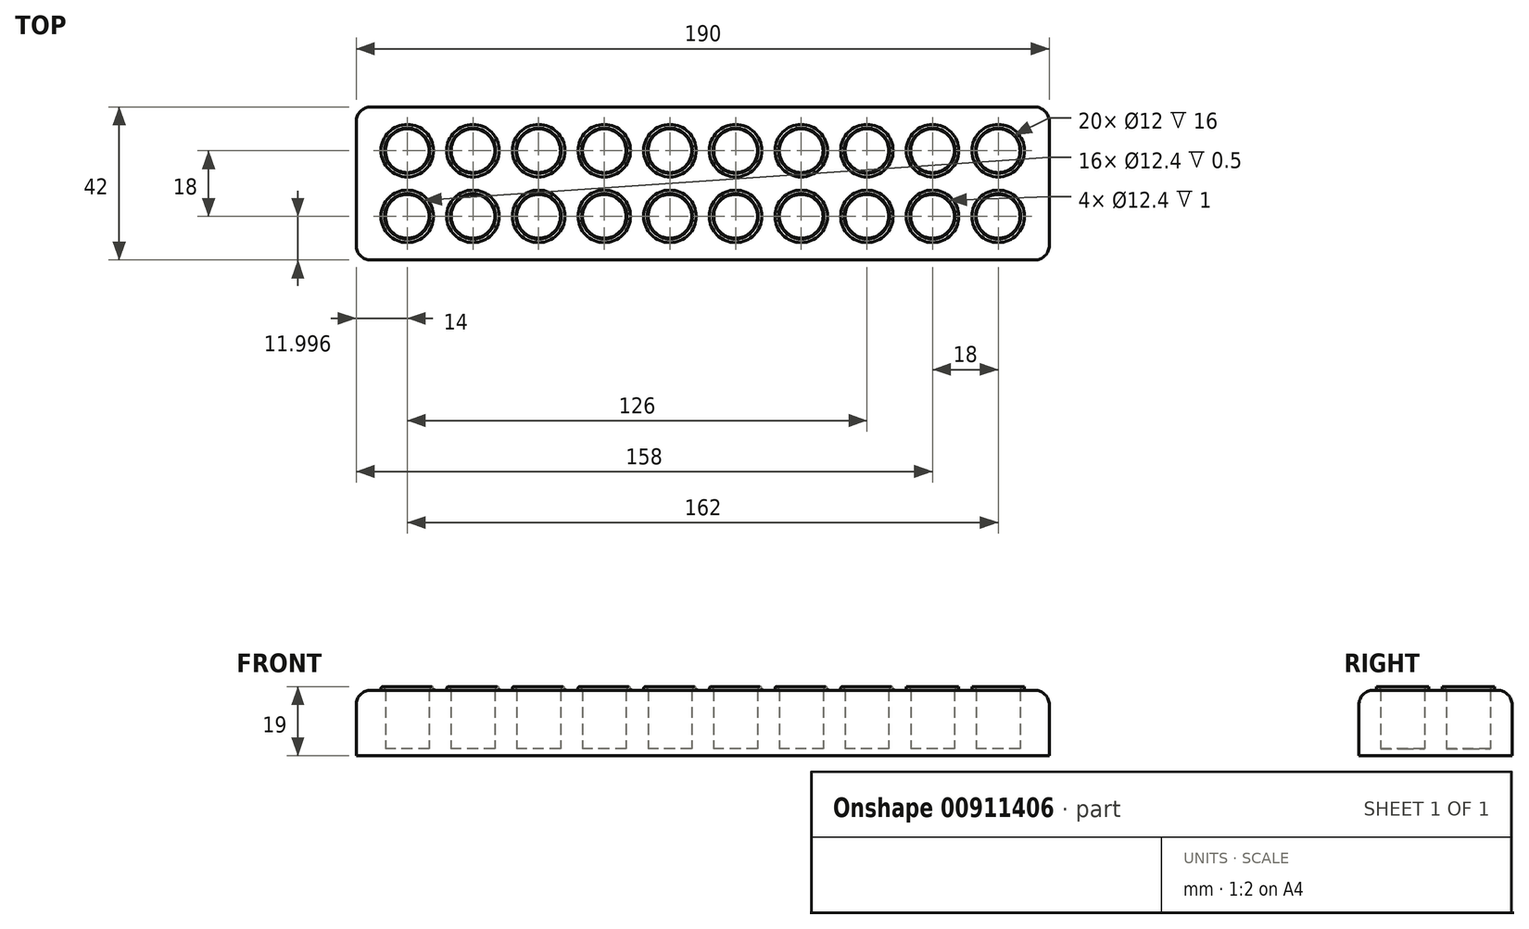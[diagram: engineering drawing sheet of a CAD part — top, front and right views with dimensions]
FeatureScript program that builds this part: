
annotation { "Feature Type Name" : "Feature", "Feature Type Description" : "" }
export const myFeature = defineFeature(function(context is Context, id is Id, definition is map)
    precondition{}
    {
        {
            var Q0;
            Q0=qCreatedBy(makeId("Top.planeOp"),FACE);
            var sketch = newSketch(context, id + "F0", { "sketchPlane" : qUnion([Q0])});
            skCircle(sketch, "E0", {"center": v(-13.55, 11.03) * mm, "radius": 6 * mm});
            skCircle(sketch, "E1.0.1.0", {"center": v(-13.55, 29.03) * mm, "radius": 6 * mm});
            skCircle(sketch, "E1.1.0.0", {"center": v(4.45, 11.03) * mm, "radius": 6 * mm});
            skCircle(sketch, "E1.1.1.0", {"center": v(4.45, 29.03) * mm, "radius": 6 * mm});
            skCircle(sketch, "E1.2.0.0", {"center": v(22.45, 11.03) * mm, "radius": 6 * mm});
            skCircle(sketch, "E1.2.1.0", {"center": v(22.45, 29.03) * mm, "radius": 6 * mm});
            skCircle(sketch, "E1.3.0.0", {"center": v(40.45, 11.03) * mm, "radius": 6 * mm});
            skCircle(sketch, "E1.3.1.0", {"center": v(40.45, 29.03) * mm, "radius": 6 * mm});
            skCircle(sketch, "E1.4.0.0", {"center": v(58.45, 11.03) * mm, "radius": 6 * mm});
            skCircle(sketch, "E1.4.1.0", {"center": v(58.45, 29.03) * mm, "radius": 6 * mm});
            skCircle(sketch, "E1.5.0.0", {"center": v(76.45, 11.03) * mm, "radius": 6 * mm});
            skCircle(sketch, "E1.5.1.0", {"center": v(76.45, 29.03) * mm, "radius": 6 * mm});
            skCircle(sketch, "E1.6.0.0", {"center": v(94.45, 11.03) * mm, "radius": 6 * mm});
            skCircle(sketch, "E1.6.1.0", {"center": v(94.45, 29.03) * mm, "radius": 6 * mm});
            skCircle(sketch, "E1.7.0.0", {"center": v(112.45, 11.03) * mm, "radius": 6 * mm});
            skCircle(sketch, "E1.7.1.0", {"center": v(112.45, 29.03) * mm, "radius": 6 * mm});
            skLineSegment(sketch, "E1.direction1", {"start": v(-13.55, 11.03) * mm, "end": v(4.45, 11.03) * mm, "construction": true});
            skLineSegment(sketch, "E1.direction2", {"start": v(-13.55, 11.03) * mm, "end": v(-13.55, 29.03) * mm, "construction": true});
            skLineSegment(sketch, "E2", {"start": v(-27.55, 41.03) * mm, "end": v(-27.55, -0.97) * mm});
            skLineSegment(sketch, "E3", {"start": v(-27.55, -0.97) * mm, "end": v(162.45, -0.97) * mm});
            skLineSegment(sketch, "E4", {"start": v(162.45, -0.97) * mm, "end": v(162.45, 41.03) * mm});
            skLineSegment(sketch, "E5", {"start": v(162.45, 41.03) * mm, "end": v(-27.55, 41.03) * mm});
            skCircle(sketch, "E6.0.8.0", {"center": v(130.45, 11.03) * mm, "radius": 6 * mm});
            skCircle(sketch, "E6.0.8.1", {"center": v(130.45, 29.03) * mm, "radius": 6 * mm});
            skCircle(sketch, "E6.0.9.0", {"center": v(148.45, 11.03) * mm, "radius": 6 * mm});
            skCircle(sketch, "E6.0.9.1", {"center": v(148.45, 29.03) * mm, "radius": 6 * mm});
            skSolve(sketch);
        }
        {
            var Q0;
            Q0 = qSketchRegion(id + "F0", true);
            extrude(context, id + "F1", {"entities" : qUnion([Q0]), "depth" : 16 * mm, "offsetDistance" : 25 * mm});
        }
        {
            var Q0;
            Q0=makeQuery(id+"F0.imprint","IMPRINT",FACE,{"disambiguationData":[TD([[makeQuery(id+"F0.imprint","IMPRINT",EDGE,{"derivedFrom":sQuery(id+"F0.wireOp",EDGE,"E0")}),-1.0]])]});
            var Q1;
            Q1=makeQuery(id+"F0.imprint","IMPRINT",FACE,{"disambiguationData":[TD([[makeQuery(id+"F0.imprint","IMPRINT",EDGE,{"derivedFrom":sQuery(id+"F0.wireOp",EDGE,"E1.1.2.0")}),1.0]])]});
            var Q2;
            Q2=makeQuery(id+"F0.imprint","IMPRINT",FACE,{"disambiguationData":[TD([[makeQuery(id+"F0.imprint","IMPRINT",EDGE,{"derivedFrom":sQuery(id+"F0.wireOp",EDGE,"E1.0.2.0")}),1.0]])]});
            var Q3;
            Q3=makeQuery(id+"F0.imprint","IMPRINT",FACE,{"disambiguationData":[TD([[makeQuery(id+"F0.imprint","IMPRINT",EDGE,{"derivedFrom":sQuery(id+"F0.wireOp",EDGE,"E1.0.1.0")}),1.0]])]});
            var Q4;
            Q4=makeQuery(id+"F0.imprint","IMPRINT",FACE,{"disambiguationData":[TD([[makeQuery(id+"F0.imprint","IMPRINT",EDGE,{"derivedFrom":sQuery(id+"F0.wireOp",EDGE,"E0")}),1.0]])]});
            var Q5;
            Q5=makeQuery(id+"F0.imprint","IMPRINT",FACE,{"disambiguationData":[TD([[makeQuery(id+"F0.imprint","IMPRINT",EDGE,{"derivedFrom":sQuery(id+"F0.wireOp",EDGE,"E1.1.0.0")}),1.0]])]});
            var Q6;
            Q6=makeQuery(id+"F0.imprint","IMPRINT",FACE,{"disambiguationData":[TD([[makeQuery(id+"F0.imprint","IMPRINT",EDGE,{"derivedFrom":sQuery(id+"F0.wireOp",EDGE,"E1.1.1.0")}),1.0]])]});
            var Q7;
            Q7=makeQuery(id+"F0.imprint","IMPRINT",FACE,{"disambiguationData":[TD([[makeQuery(id+"F0.imprint","IMPRINT",EDGE,{"derivedFrom":sQuery(id+"F0.wireOp",EDGE,"E1.1.3.0")}),1.0]])]});
            var Q8;
            Q8=makeQuery(id+"F0.imprint","IMPRINT",FACE,{"disambiguationData":[TD([[makeQuery(id+"F0.imprint","IMPRINT",EDGE,{"derivedFrom":sQuery(id+"F0.wireOp",EDGE,"E1.0.3.0")}),1.0]])]});
            var Q9;
            Q9=makeQuery(id+"F0.imprint","IMPRINT",FACE,{"disambiguationData":[TD([[makeQuery(id+"F0.imprint","IMPRINT",EDGE,{"derivedFrom":sQuery(id+"F0.wireOp",EDGE,"E1.2.2.0")}),1.0]])]});
            var Q10;
            Q10=makeQuery(id+"F0.imprint","IMPRINT",FACE,{"disambiguationData":[TD([[makeQuery(id+"F0.imprint","IMPRINT",EDGE,{"derivedFrom":sQuery(id+"F0.wireOp",EDGE,"E1.2.1.0")}),1.0]])]});
            var Q11;
            Q11=makeQuery(id+"F0.imprint","IMPRINT",FACE,{"disambiguationData":[TD([[makeQuery(id+"F0.imprint","IMPRINT",EDGE,{"derivedFrom":sQuery(id+"F0.wireOp",EDGE,"E1.2.0.0")}),1.0]])]});
            var Q12;
            Q12=makeQuery(id+"F0.imprint","IMPRINT",FACE,{"disambiguationData":[TD([[makeQuery(id+"F0.imprint","IMPRINT",EDGE,{"derivedFrom":sQuery(id+"F0.wireOp",EDGE,"E1.2.3.0")}),1.0]])]});
            var Q13;
            Q13=makeQuery(id+"F0.imprint","IMPRINT",FACE,{"disambiguationData":[TD([[makeQuery(id+"F0.imprint","IMPRINT",EDGE,{"derivedFrom":sQuery(id+"F0.wireOp",EDGE,"E1.3.3.0")}),1.0]])]});
            var Q14;
            Q14=makeQuery(id+"F0.imprint","IMPRINT",FACE,{"disambiguationData":[TD([[makeQuery(id+"F0.imprint","IMPRINT",EDGE,{"derivedFrom":sQuery(id+"F0.wireOp",EDGE,"E1.3.2.0")}),1.0]])]});
            var Q15;
            Q15=makeQuery(id+"F0.imprint","IMPRINT",FACE,{"disambiguationData":[TD([[makeQuery(id+"F0.imprint","IMPRINT",EDGE,{"derivedFrom":sQuery(id+"F0.wireOp",EDGE,"E1.3.1.0")}),1.0]])]});
            var Q16;
            Q16=makeQuery(id+"F0.imprint","IMPRINT",FACE,{"disambiguationData":[TD([[makeQuery(id+"F0.imprint","IMPRINT",EDGE,{"derivedFrom":sQuery(id+"F0.wireOp",EDGE,"E1.3.0.0")}),1.0]])]});
            var Q17;
            Q17=makeQuery(id+"F0.imprint","IMPRINT",FACE,{"disambiguationData":[TD([[makeQuery(id+"F0.imprint","IMPRINT",EDGE,{"derivedFrom":sQuery(id+"F0.wireOp",EDGE,"E1.4.0.0")}),1.0]])]});
            var Q18;
            Q18=makeQuery(id+"F0.imprint","IMPRINT",FACE,{"disambiguationData":[TD([[makeQuery(id+"F0.imprint","IMPRINT",EDGE,{"derivedFrom":sQuery(id+"F0.wireOp",EDGE,"E1.4.1.0")}),1.0]])]});
            var Q19;
            Q19=makeQuery(id+"F0.imprint","IMPRINT",FACE,{"disambiguationData":[TD([[makeQuery(id+"F0.imprint","IMPRINT",EDGE,{"derivedFrom":sQuery(id+"F0.wireOp",EDGE,"E1.4.2.0")}),1.0]])]});
            var Q20;
            Q20=makeQuery(id+"F0.imprint","IMPRINT",FACE,{"disambiguationData":[TD([[makeQuery(id+"F0.imprint","IMPRINT",EDGE,{"derivedFrom":sQuery(id+"F0.wireOp",EDGE,"E1.4.3.0")}),1.0]])]});
            var Q21;
            Q21=makeQuery(id+"F0.imprint","IMPRINT",FACE,{"disambiguationData":[TD([[makeQuery(id+"F0.imprint","IMPRINT",EDGE,{"derivedFrom":sQuery(id+"F0.wireOp",EDGE,"E1.5.3.0")}),1.0]])]});
            var Q22;
            Q22=makeQuery(id+"F0.imprint","IMPRINT",FACE,{"disambiguationData":[TD([[makeQuery(id+"F0.imprint","IMPRINT",EDGE,{"derivedFrom":sQuery(id+"F0.wireOp",EDGE,"E1.5.2.0")}),1.0]])]});
            var Q23;
            Q23=makeQuery(id+"F0.imprint","IMPRINT",FACE,{"disambiguationData":[TD([[makeQuery(id+"F0.imprint","IMPRINT",EDGE,{"derivedFrom":sQuery(id+"F0.wireOp",EDGE,"E1.5.1.0")}),1.0]])]});
            var Q24;
            Q24=makeQuery(id+"F0.imprint","IMPRINT",FACE,{"disambiguationData":[TD([[makeQuery(id+"F0.imprint","IMPRINT",EDGE,{"derivedFrom":sQuery(id+"F0.wireOp",EDGE,"E1.5.0.0")}),1.0]])]});
            var Q25;
            Q25=makeQuery(id+"F0.imprint","IMPRINT",FACE,{"disambiguationData":[TD([[makeQuery(id+"F0.imprint","IMPRINT",EDGE,{"derivedFrom":sQuery(id+"F0.wireOp",EDGE,"E1.6.0.0")}),1.0]])]});
            var Q26;
            Q26=makeQuery(id+"F0.imprint","IMPRINT",FACE,{"disambiguationData":[TD([[makeQuery(id+"F0.imprint","IMPRINT",EDGE,{"derivedFrom":sQuery(id+"F0.wireOp",EDGE,"E1.6.2.0")}),1.0]])]});
            var Q27;
            Q27=makeQuery(id+"F0.imprint","IMPRINT",FACE,{"disambiguationData":[TD([[makeQuery(id+"F0.imprint","IMPRINT",EDGE,{"derivedFrom":sQuery(id+"F0.wireOp",EDGE,"E1.6.1.0")}),1.0]])]});
            var Q28;
            Q28=makeQuery(id+"F0.imprint","IMPRINT",FACE,{"disambiguationData":[TD([[makeQuery(id+"F0.imprint","IMPRINT",EDGE,{"derivedFrom":sQuery(id+"F0.wireOp",EDGE,"E1.6.3.0")}),1.0]])]});
            var Q29;
            Q29=makeQuery(id+"F0.imprint","IMPRINT",FACE,{"disambiguationData":[TD([[makeQuery(id+"F0.imprint","IMPRINT",EDGE,{"derivedFrom":sQuery(id+"F0.wireOp",EDGE,"E1.7.3.0")}),1.0]])]});
            var Q30;
            Q30=makeQuery(id+"F0.imprint","IMPRINT",FACE,{"disambiguationData":[TD([[makeQuery(id+"F0.imprint","IMPRINT",EDGE,{"derivedFrom":sQuery(id+"F0.wireOp",EDGE,"E1.7.2.0")}),1.0]])]});
            var Q31;
            Q31=makeQuery(id+"F0.imprint","IMPRINT",FACE,{"disambiguationData":[TD([[makeQuery(id+"F0.imprint","IMPRINT",EDGE,{"derivedFrom":sQuery(id+"F0.wireOp",EDGE,"E1.7.1.0")}),1.0]])]});
            var Q32;
            Q32=makeQuery(id+"F0.imprint","IMPRINT",FACE,{"disambiguationData":[TD([[makeQuery(id+"F0.imprint","IMPRINT",EDGE,{"derivedFrom":sQuery(id+"F0.wireOp",EDGE,"E1.7.0.0")}),1.0]])]});
            var Q33;
            Q33=makeQuery(id+"F0.imprint","IMPRINT",FACE,{"disambiguationData":[TD([[makeQuery(id+"F0.imprint","IMPRINT",EDGE,{"derivedFrom":sQuery(id+"F0.wireOp",EDGE,"2ea0dcad-b240-4836-abf1-8ca867a6ec1d.0.0.4")}),1.0]])]});
            var Q34;
            Q34=makeQuery(id+"F0.imprint","IMPRINT",FACE,{"disambiguationData":[TD([[makeQuery(id+"F0.imprint","IMPRINT",EDGE,{"derivedFrom":sQuery(id+"F0.wireOp",EDGE,"2ea0dcad-b240-4836-abf1-8ca867a6ec1d.0.1.4")}),1.0]])]});
            var Q35;
            Q35=makeQuery(id+"F0.imprint","IMPRINT",FACE,{"disambiguationData":[TD([[makeQuery(id+"F0.imprint","IMPRINT",EDGE,{"derivedFrom":sQuery(id+"F0.wireOp",EDGE,"2ea0dcad-b240-4836-abf1-8ca867a6ec1d.0.2.4")}),1.0]])]});
            var Q36;
            Q36=makeQuery(id+"F0.imprint","IMPRINT",FACE,{"disambiguationData":[TD([[makeQuery(id+"F0.imprint","IMPRINT",EDGE,{"derivedFrom":sQuery(id+"F0.wireOp",EDGE,"2ea0dcad-b240-4836-abf1-8ca867a6ec1d.0.3.4")}),1.0]])]});
            var Q37;
            Q37=makeQuery(id+"F0.imprint","IMPRINT",FACE,{"disambiguationData":[TD([[makeQuery(id+"F0.imprint","IMPRINT",EDGE,{"derivedFrom":sQuery(id+"F0.wireOp",EDGE,"2ea0dcad-b240-4836-abf1-8ca867a6ec1d.0.4.4")}),1.0]])]});
            var Q38;
            Q38=makeQuery(id+"F0.imprint","IMPRINT",FACE,{"disambiguationData":[TD([[makeQuery(id+"F0.imprint","IMPRINT",EDGE,{"derivedFrom":sQuery(id+"F0.wireOp",EDGE,"2ea0dcad-b240-4836-abf1-8ca867a6ec1d.0.5.4")}),1.0]])]});
            var Q39;
            Q39=makeQuery(id+"F0.imprint","IMPRINT",FACE,{"disambiguationData":[TD([[makeQuery(id+"F0.imprint","IMPRINT",EDGE,{"derivedFrom":sQuery(id+"F0.wireOp",EDGE,"2ea0dcad-b240-4836-abf1-8ca867a6ec1d.0.6.4")}),1.0]])]});
            var Q40;
            Q40=makeQuery(id+"F0.imprint","IMPRINT",FACE,{"disambiguationData":[TD([[makeQuery(id+"F0.imprint","IMPRINT",EDGE,{"derivedFrom":sQuery(id+"F0.wireOp",EDGE,"2ea0dcad-b240-4836-abf1-8ca867a6ec1d.0.7.4")}),1.0]])]});
            var Q41;
            Q41=makeQuery(id+"F0.imprint","IMPRINT",FACE,{"disambiguationData":[TD([[makeQuery(id+"F0.imprint","IMPRINT",EDGE,{"derivedFrom":sQuery(id+"F0.wireOp",EDGE,"2ea0dcad-b240-4836-abf1-8ca867a6ec1d.0.8.4")}),1.0]])]});
            var Q42;
            Q42=makeQuery(id+"F0.imprint","IMPRINT",FACE,{"disambiguationData":[TD([[makeQuery(id+"F0.imprint","IMPRINT",EDGE,{"derivedFrom":sQuery(id+"F0.wireOp",EDGE,"E6.0.8.3")}),1.0]])]});
            var Q43;
            Q43=makeQuery(id+"F0.imprint","IMPRINT",FACE,{"disambiguationData":[TD([[makeQuery(id+"F0.imprint","IMPRINT",EDGE,{"derivedFrom":sQuery(id+"F0.wireOp",EDGE,"E6.0.8.2")}),1.0]])]});
            var Q44;
            Q44=makeQuery(id+"F0.imprint","IMPRINT",FACE,{"disambiguationData":[TD([[makeQuery(id+"F0.imprint","IMPRINT",EDGE,{"derivedFrom":sQuery(id+"F0.wireOp",EDGE,"E6.0.8.1")}),1.0]])]});
            var Q45;
            Q45=makeQuery(id+"F0.imprint","IMPRINT",FACE,{"disambiguationData":[TD([[makeQuery(id+"F0.imprint","IMPRINT",EDGE,{"derivedFrom":sQuery(id+"F0.wireOp",EDGE,"E6.0.8.0")}),1.0]])]});
            var Q46;
            Q46=makeQuery(id+"F0.imprint","IMPRINT",FACE,{"disambiguationData":[TD([[makeQuery(id+"F0.imprint","IMPRINT",EDGE,{"derivedFrom":sQuery(id+"F0.wireOp",EDGE,"E6.0.9.0")}),1.0]])]});
            var Q47;
            Q47=makeQuery(id+"F0.imprint","IMPRINT",FACE,{"disambiguationData":[TD([[makeQuery(id+"F0.imprint","IMPRINT",EDGE,{"derivedFrom":sQuery(id+"F0.wireOp",EDGE,"E6.0.9.1")}),1.0]])]});
            var Q48;
            Q48=makeQuery(id+"F0.imprint","IMPRINT",FACE,{"disambiguationData":[TD([[makeQuery(id+"F0.imprint","IMPRINT",EDGE,{"derivedFrom":sQuery(id+"F0.wireOp",EDGE,"E6.0.9.2")}),1.0]])]});
            var Q49;
            Q49=makeQuery(id+"F0.imprint","IMPRINT",FACE,{"disambiguationData":[TD([[makeQuery(id+"F0.imprint","IMPRINT",EDGE,{"derivedFrom":sQuery(id+"F0.wireOp",EDGE,"E6.0.9.3")}),1.0]])]});
            var Q50;
            Q50=makeQuery(id+"F0.imprint","IMPRINT",FACE,{"disambiguationData":[TD([[makeQuery(id+"F0.imprint","IMPRINT",EDGE,{"derivedFrom":sQuery(id+"F0.wireOp",EDGE,"2ea0dcad-b240-4836-abf1-8ca867a6ec1d.0.9.4")}),1.0]])]});
            extrude(context, id + "F2", {"entities" : qUnion([Q0, Q1, Q2, Q3, Q4, Q5, Q6, Q7, Q8, Q9, Q10, Q11, Q12, Q13, Q14, Q15, Q16, Q17, Q18, Q19, Q20, Q21, Q22, Q23, Q24, Q25, Q26, Q27, Q28, Q29, Q30, Q31, Q32, Q33, Q34, Q35, Q36, Q37, Q38, Q39, Q40, Q41, Q42, Q43, Q44, Q45, Q46, Q47, Q48, Q49, Q50]), "operationType" : NewBodyOperationType.ADD, "oppositeDirection" : true, "depth" : 2 * mm, "offsetDistance" : 25 * mm});
        }
        {
            var Q0;
            Q0=makeQuery(id+"F1.opExtrude","CAP_EDGE",EDGE,{"disambiguationData":[OSD([sQuery(id+"F0.wireOp",EDGE,"E3")])],"isStart":false});
            var Q1;
            Q1=makeQuery(id+"F1.opExtrude","CAP_EDGE",EDGE,{"disambiguationData":[OSD([sQuery(id+"F0.wireOp",EDGE,"E4")])],"isStart":false});
            var Q2;
            Q2=makeQuery(id+"F1.opExtrude","CAP_EDGE",EDGE,{"disambiguationData":[OSD([sQuery(id+"F0.wireOp",EDGE,"E5")])],"isStart":false});
            var Q3;
            Q3=makeQuery(id+"F1.opExtrude","CAP_EDGE",EDGE,{"disambiguationData":[OSD([sQuery(id+"F0.wireOp",EDGE,"E2")])],"isStart":false});
            var Q4;
            {var subQ0=sQuery(id+"F0.wireOp",EDGE,"E5");var subQ1=sQuery(id+"F0.wireOp",EDGE,"E2");Q4=makeQuery(id+"F2.boolean.opBoolean","MERGE",EDGE,{"derivedFrom":[makeQuery(id+"F1.opExtrude","SWEPT_EDGE",EDGE,{"disambiguationData":[OSD([subQ1,subQ0])]}),makeQuery(id+"F2.opExtrude","SWEPT_EDGE",EDGE,{"disambiguationData":[OSD([subQ1,subQ0])]})]});}
            var Q5;
            {var subQ0=sQuery(id+"F0.wireOp",EDGE,"E5");var subQ1=sQuery(id+"F0.wireOp",EDGE,"E4");Q5=makeQuery(id+"F2.boolean.opBoolean","MERGE",EDGE,{"derivedFrom":[makeQuery(id+"F1.opExtrude","SWEPT_EDGE",EDGE,{"disambiguationData":[OSD([subQ1,subQ0])]}),makeQuery(id+"F2.opExtrude","SWEPT_EDGE",EDGE,{"disambiguationData":[OSD([subQ1,subQ0])]})]});}
            var Q6;
            {var subQ0=sQuery(id+"F0.wireOp",EDGE,"E3");var subQ1=sQuery(id+"F0.wireOp",EDGE,"E2");Q6=makeQuery(id+"F2.boolean.opBoolean","MERGE",EDGE,{"derivedFrom":[makeQuery(id+"F1.opExtrude","SWEPT_EDGE",EDGE,{"disambiguationData":[OSD([subQ1,subQ0])]}),makeQuery(id+"F2.opExtrude","SWEPT_EDGE",EDGE,{"disambiguationData":[OSD([subQ1,subQ0])]})]});}
            var Q7;
            {var subQ0=sQuery(id+"F0.wireOp",EDGE,"E4");var subQ1=sQuery(id+"F0.wireOp",EDGE,"E3");Q7=makeQuery(id+"F2.boolean.opBoolean","MERGE",EDGE,{"derivedFrom":[makeQuery(id+"F1.opExtrude","SWEPT_EDGE",EDGE,{"disambiguationData":[OSD([subQ1,subQ0])]}),makeQuery(id+"F2.opExtrude","SWEPT_EDGE",EDGE,{"disambiguationData":[OSD([subQ1,subQ0])]})]});}
            fillet(context, id + "F3", {"entities" : qUnion([Q0, Q1, Q2, Q3, Q4, Q5, Q6, Q7]), "radius" : 4 * mm, "tangentPropagation" : true, "allowEdgeOverflow" : false});
        }
        {
            var Q0;
            Q0=makeQuery(id+"F1.opExtrude","CAP_FACE",FACE,{"disambiguationData":[OSD([sQuery(id+"F0.wireOp",EDGE,"E0"),sQuery(id+"F0.wireOp",EDGE,"E1.0.1.0"),sQuery(id+"F0.wireOp",EDGE,"E1.0.2.0"),sQuery(id+"F0.wireOp",EDGE,"E1.0.3.0"),sQuery(id+"F0.wireOp",EDGE,"E1.1.0.0"),sQuery(id+"F0.wireOp",EDGE,"E1.1.1.0"),sQuery(id+"F0.wireOp",EDGE,"E1.1.2.0"),sQuery(id+"F0.wireOp",EDGE,"E1.1.3.0"),sQuery(id+"F0.wireOp",EDGE,"E1.2.0.0"),sQuery(id+"F0.wireOp",EDGE,"E1.2.1.0"),sQuery(id+"F0.wireOp",EDGE,"E1.2.2.0"),sQuery(id+"F0.wireOp",EDGE,"E1.2.3.0"),sQuery(id+"F0.wireOp",EDGE,"E1.3.0.0"),sQuery(id+"F0.wireOp",EDGE,"E1.3.1.0"),sQuery(id+"F0.wireOp",EDGE,"E1.3.2.0"),sQuery(id+"F0.wireOp",EDGE,"E1.3.3.0"),sQuery(id+"F0.wireOp",EDGE,"E1.4.0.0"),sQuery(id+"F0.wireOp",EDGE,"E1.4.1.0"),sQuery(id+"F0.wireOp",EDGE,"E1.4.2.0"),sQuery(id+"F0.wireOp",EDGE,"E1.4.3.0"),sQuery(id+"F0.wireOp",EDGE,"E1.5.0.0"),sQuery(id+"F0.wireOp",EDGE,"E1.5.1.0"),sQuery(id+"F0.wireOp",EDGE,"E1.5.2.0"),sQuery(id+"F0.wireOp",EDGE,"E1.5.3.0"),sQuery(id+"F0.wireOp",EDGE,"E1.6.0.0"),sQuery(id+"F0.wireOp",EDGE,"E1.6.1.0"),sQuery(id+"F0.wireOp",EDGE,"E1.6.2.0"),sQuery(id+"F0.wireOp",EDGE,"E1.6.3.0"),sQuery(id+"F0.wireOp",EDGE,"E1.7.0.0"),sQuery(id+"F0.wireOp",EDGE,"E1.7.1.0"),sQuery(id+"F0.wireOp",EDGE,"E1.7.2.0"),sQuery(id+"F0.wireOp",EDGE,"E1.7.3.0"),sQuery(id+"F0.wireOp",EDGE,"E2"),sQuery(id+"F0.wireOp",EDGE,"E3"),sQuery(id+"F0.wireOp",EDGE,"E4"),sQuery(id+"F0.wireOp",EDGE,"E5")])],"isStart":false});
            var sketch = newSketch(context, id + "F4", { "sketchPlane" : qUnion([Q0])});
            skCircle(sketch, "E7", {"center": v(-13.55, 11.03) * mm, "radius": 7.2 * mm});
            skCircle(sketch, "E8", {"center": v(-13.55, 11.03) * mm, "radius": 6.2 * mm});
            skCircle(sketch, "E9.0.1.0", {"center": v(-13.55, 29.03) * mm, "radius": 7.2 * mm});
            skCircle(sketch, "E9.0.1.1", {"center": v(-13.55, 29.03) * mm, "radius": 6.2 * mm});
            skCircle(sketch, "E9.1.0.0", {"center": v(4.45, 11.03) * mm, "radius": 7.2 * mm});
            skCircle(sketch, "E9.1.0.1", {"center": v(4.45, 11.03) * mm, "radius": 6.2 * mm});
            skCircle(sketch, "E9.1.1.0", {"center": v(4.45, 29.03) * mm, "radius": 7.2 * mm});
            skCircle(sketch, "E9.1.1.1", {"center": v(4.45, 29.03) * mm, "radius": 6.2 * mm});
            skCircle(sketch, "E9.2.0.0", {"center": v(22.45, 11.03) * mm, "radius": 7.2 * mm});
            skCircle(sketch, "E9.2.0.1", {"center": v(22.45, 11.03) * mm, "radius": 6.2 * mm});
            skCircle(sketch, "E9.2.1.0", {"center": v(22.45, 29.03) * mm, "radius": 7.2 * mm});
            skCircle(sketch, "E9.2.1.1", {"center": v(22.45, 29.03) * mm, "radius": 6.2 * mm});
            skCircle(sketch, "E9.3.0.0", {"center": v(40.45, 11.03) * mm, "radius": 7.2 * mm});
            skCircle(sketch, "E9.3.0.1", {"center": v(40.45, 11.03) * mm, "radius": 6.2 * mm});
            skCircle(sketch, "E9.3.1.0", {"center": v(40.45, 29.03) * mm, "radius": 7.2 * mm});
            skCircle(sketch, "E9.3.1.1", {"center": v(40.45, 29.03) * mm, "radius": 6.2 * mm});
            skCircle(sketch, "E9.4.0.0", {"center": v(58.45, 11.03) * mm, "radius": 7.2 * mm});
            skCircle(sketch, "E9.4.0.1", {"center": v(58.45, 11.03) * mm, "radius": 6.2 * mm});
            skCircle(sketch, "E9.4.1.0", {"center": v(58.45, 29.03) * mm, "radius": 7.2 * mm});
            skCircle(sketch, "E9.4.1.1", {"center": v(58.45, 29.03) * mm, "radius": 6.2 * mm});
            skCircle(sketch, "E9.5.0.0", {"center": v(76.45, 11.03) * mm, "radius": 7.2 * mm});
            skCircle(sketch, "E9.5.0.1", {"center": v(76.45, 11.03) * mm, "radius": 6.2 * mm});
            skCircle(sketch, "E9.5.1.0", {"center": v(76.45, 29.03) * mm, "radius": 7.2 * mm});
            skCircle(sketch, "E9.5.1.1", {"center": v(76.45, 29.03) * mm, "radius": 6.2 * mm});
            skCircle(sketch, "E9.6.0.0", {"center": v(94.45, 11.03) * mm, "radius": 7.2 * mm});
            skCircle(sketch, "E9.6.0.1", {"center": v(94.45, 11.03) * mm, "radius": 6.2 * mm});
            skCircle(sketch, "E9.6.1.0", {"center": v(94.45, 29.03) * mm, "radius": 7.2 * mm});
            skCircle(sketch, "E9.6.1.1", {"center": v(94.45, 29.03) * mm, "radius": 6.2 * mm});
            skCircle(sketch, "E9.7.0.0", {"center": v(112.45, 11.03) * mm, "radius": 7.2 * mm});
            skCircle(sketch, "E9.7.0.1", {"center": v(112.45, 11.03) * mm, "radius": 6.2 * mm});
            skCircle(sketch, "E9.7.1.0", {"center": v(112.45, 29.03) * mm, "radius": 7.2 * mm});
            skCircle(sketch, "E9.7.1.1", {"center": v(112.45, 29.03) * mm, "radius": 6.2 * mm});
            skLineSegment(sketch, "E9.direction1", {"start": v(-13.55, 11.03) * mm, "end": v(4.45, 11.03) * mm, "construction": true});
            skLineSegment(sketch, "E9.direction2", {"start": v(-13.55, 11.03) * mm, "end": v(-13.55, 29.03) * mm, "construction": true});
            skCircle(sketch, "E10.0.8.0", {"center": v(130.45, 11.03) * mm, "radius": 7.2 * mm});
            skCircle(sketch, "E10.2.8.0", {"center": v(130.45, 11.03) * mm, "radius": 6.2 * mm});
            skCircle(sketch, "E10.0.8.1", {"center": v(130.45, 29.03) * mm, "radius": 7.2 * mm});
            skCircle(sketch, "E10.2.8.1", {"center": v(130.45, 29.03) * mm, "radius": 6.2 * mm});
            skCircle(sketch, "E10.0.9.0", {"center": v(148.45, 11.03) * mm, "radius": 7.2 * mm});
            skCircle(sketch, "E10.2.9.0", {"center": v(148.45, 11.03) * mm, "radius": 6.2 * mm});
            skCircle(sketch, "E10.0.9.1", {"center": v(148.45, 29.03) * mm, "radius": 7.2 * mm});
            skCircle(sketch, "E10.2.9.1", {"center": v(148.45, 29.03) * mm, "radius": 6.2 * mm});
            skSolve(sketch);
        }
        {
            var Q0;
            Q0=makeQuery(id+"F4.imprint","IMPRINT",FACE,{"disambiguationData":[TD([[makeQuery(id+"F4.imprint","IMPRINT",EDGE,{"derivedFrom":sQuery(id+"F4.wireOp",EDGE,"E7")}),1.0]])]});
            var Q1;
            Q1=makeQuery(id+"F4.imprint","IMPRINT",FACE,{"disambiguationData":[TD([[makeQuery(id+"F4.imprint","IMPRINT",EDGE,{"derivedFrom":sQuery(id+"F4.wireOp",EDGE,"E9.0.1.0")}),1.0]])]});
            var Q2;
            Q2=makeQuery(id+"F4.imprint","IMPRINT",FACE,{"disambiguationData":[TD([[makeQuery(id+"F4.imprint","IMPRINT",EDGE,{"derivedFrom":sQuery(id+"F4.wireOp",EDGE,"E9.1.1.0")}),1.0]])]});
            var Q3;
            Q3=makeQuery(id+"F4.imprint","IMPRINT",FACE,{"disambiguationData":[TD([[makeQuery(id+"F4.imprint","IMPRINT",EDGE,{"derivedFrom":sQuery(id+"F4.wireOp",EDGE,"E9.1.0.0")}),1.0]])]});
            var Q4;
            Q4=makeQuery(id+"F4.imprint","IMPRINT",FACE,{"disambiguationData":[TD([[makeQuery(id+"F4.imprint","IMPRINT",EDGE,{"derivedFrom":sQuery(id+"F4.wireOp",EDGE,"E9.0.2.0")}),1.0]])]});
            var Q5;
            Q5=makeQuery(id+"F4.imprint","IMPRINT",FACE,{"disambiguationData":[TD([[makeQuery(id+"F4.imprint","IMPRINT",EDGE,{"derivedFrom":sQuery(id+"F4.wireOp",EDGE,"E9.1.2.0")}),1.0]])]});
            var Q6;
            Q6=makeQuery(id+"F4.imprint","IMPRINT",FACE,{"disambiguationData":[TD([[makeQuery(id+"F4.imprint","IMPRINT",EDGE,{"derivedFrom":sQuery(id+"F4.wireOp",EDGE,"E9.0.3.0")}),1.0]])]});
            var Q7;
            Q7=makeQuery(id+"F4.imprint","IMPRINT",FACE,{"disambiguationData":[TD([[makeQuery(id+"F4.imprint","IMPRINT",EDGE,{"derivedFrom":sQuery(id+"F4.wireOp",EDGE,"E9.1.3.0")}),1.0]])]});
            var Q8;
            Q8=makeQuery(id+"F4.imprint","IMPRINT",FACE,{"disambiguationData":[TD([[makeQuery(id+"F4.imprint","IMPRINT",EDGE,{"derivedFrom":sQuery(id+"F4.wireOp",EDGE,"E9.2.3.0")}),1.0]])]});
            var Q9;
            Q9=makeQuery(id+"F4.imprint","IMPRINT",FACE,{"disambiguationData":[TD([[makeQuery(id+"F4.imprint","IMPRINT",EDGE,{"derivedFrom":sQuery(id+"F4.wireOp",EDGE,"E9.2.2.0")}),1.0]])]});
            var Q10;
            Q10=makeQuery(id+"F4.imprint","IMPRINT",FACE,{"disambiguationData":[TD([[makeQuery(id+"F4.imprint","IMPRINT",EDGE,{"derivedFrom":sQuery(id+"F4.wireOp",EDGE,"E9.2.1.0")}),1.0]])]});
            var Q11;
            Q11=makeQuery(id+"F4.imprint","IMPRINT",FACE,{"disambiguationData":[TD([[makeQuery(id+"F4.imprint","IMPRINT",EDGE,{"derivedFrom":sQuery(id+"F4.wireOp",EDGE,"E9.2.0.0")}),1.0]])]});
            var Q12;
            Q12=makeQuery(id+"F4.imprint","IMPRINT",FACE,{"disambiguationData":[TD([[makeQuery(id+"F4.imprint","IMPRINT",EDGE,{"derivedFrom":sQuery(id+"F4.wireOp",EDGE,"E9.3.0.0")}),1.0]])]});
            var Q13;
            Q13=makeQuery(id+"F4.imprint","IMPRINT",FACE,{"disambiguationData":[TD([[makeQuery(id+"F4.imprint","IMPRINT",EDGE,{"derivedFrom":sQuery(id+"F4.wireOp",EDGE,"E9.3.1.0")}),1.0]])]});
            var Q14;
            Q14=makeQuery(id+"F4.imprint","IMPRINT",FACE,{"disambiguationData":[TD([[makeQuery(id+"F4.imprint","IMPRINT",EDGE,{"derivedFrom":sQuery(id+"F4.wireOp",EDGE,"E9.3.2.0")}),1.0]])]});
            var Q15;
            Q15=makeQuery(id+"F4.imprint","IMPRINT",FACE,{"disambiguationData":[TD([[makeQuery(id+"F4.imprint","IMPRINT",EDGE,{"derivedFrom":sQuery(id+"F4.wireOp",EDGE,"E9.3.3.0")}),1.0]])]});
            var Q16;
            Q16=makeQuery(id+"F4.imprint","IMPRINT",FACE,{"disambiguationData":[TD([[makeQuery(id+"F4.imprint","IMPRINT",EDGE,{"derivedFrom":sQuery(id+"F4.wireOp",EDGE,"E9.4.0.0")}),1.0]])]});
            var Q17;
            Q17=makeQuery(id+"F4.imprint","IMPRINT",FACE,{"disambiguationData":[TD([[makeQuery(id+"F4.imprint","IMPRINT",EDGE,{"derivedFrom":sQuery(id+"F4.wireOp",EDGE,"E9.4.1.0")}),1.0]])]});
            var Q18;
            Q18=makeQuery(id+"F4.imprint","IMPRINT",FACE,{"disambiguationData":[TD([[makeQuery(id+"F4.imprint","IMPRINT",EDGE,{"derivedFrom":sQuery(id+"F4.wireOp",EDGE,"E9.4.2.0")}),1.0]])]});
            var Q19;
            Q19=makeQuery(id+"F4.imprint","IMPRINT",FACE,{"disambiguationData":[TD([[makeQuery(id+"F4.imprint","IMPRINT",EDGE,{"derivedFrom":sQuery(id+"F4.wireOp",EDGE,"E9.4.3.0")}),1.0]])]});
            var Q20;
            Q20=makeQuery(id+"F4.imprint","IMPRINT",FACE,{"disambiguationData":[TD([[makeQuery(id+"F4.imprint","IMPRINT",EDGE,{"derivedFrom":sQuery(id+"F4.wireOp",EDGE,"E9.5.3.0")}),1.0]])]});
            var Q21;
            Q21=makeQuery(id+"F4.imprint","IMPRINT",FACE,{"disambiguationData":[TD([[makeQuery(id+"F4.imprint","IMPRINT",EDGE,{"derivedFrom":sQuery(id+"F4.wireOp",EDGE,"E9.5.2.0")}),1.0]])]});
            var Q22;
            Q22=makeQuery(id+"F4.imprint","IMPRINT",FACE,{"disambiguationData":[TD([[makeQuery(id+"F4.imprint","IMPRINT",EDGE,{"derivedFrom":sQuery(id+"F4.wireOp",EDGE,"E9.5.1.0")}),1.0]])]});
            var Q23;
            Q23=makeQuery(id+"F4.imprint","IMPRINT",FACE,{"disambiguationData":[TD([[makeQuery(id+"F4.imprint","IMPRINT",EDGE,{"derivedFrom":sQuery(id+"F4.wireOp",EDGE,"E9.5.0.0")}),1.0]])]});
            var Q24;
            Q24=makeQuery(id+"F4.imprint","IMPRINT",FACE,{"disambiguationData":[TD([[makeQuery(id+"F4.imprint","IMPRINT",EDGE,{"derivedFrom":sQuery(id+"F4.wireOp",EDGE,"E9.6.0.0")}),1.0]])]});
            var Q25;
            Q25=makeQuery(id+"F4.imprint","IMPRINT",FACE,{"disambiguationData":[TD([[makeQuery(id+"F4.imprint","IMPRINT",EDGE,{"derivedFrom":sQuery(id+"F4.wireOp",EDGE,"E9.7.0.0")}),1.0]])]});
            var Q26;
            Q26=makeQuery(id+"F4.imprint","IMPRINT",FACE,{"disambiguationData":[TD([[makeQuery(id+"F4.imprint","IMPRINT",EDGE,{"derivedFrom":sQuery(id+"F4.wireOp",EDGE,"E9.7.1.0")}),1.0]])]});
            var Q27;
            Q27=makeQuery(id+"F4.imprint","IMPRINT",FACE,{"disambiguationData":[TD([[makeQuery(id+"F4.imprint","IMPRINT",EDGE,{"derivedFrom":sQuery(id+"F4.wireOp",EDGE,"E9.6.1.0")}),1.0]])]});
            var Q28;
            Q28=makeQuery(id+"F4.imprint","IMPRINT",FACE,{"disambiguationData":[TD([[makeQuery(id+"F4.imprint","IMPRINT",EDGE,{"derivedFrom":sQuery(id+"F4.wireOp",EDGE,"E9.7.2.0")}),1.0]])]});
            var Q29;
            Q29=makeQuery(id+"F4.imprint","IMPRINT",FACE,{"disambiguationData":[TD([[makeQuery(id+"F4.imprint","IMPRINT",EDGE,{"derivedFrom":sQuery(id+"F4.wireOp",EDGE,"E9.6.2.0")}),1.0]])]});
            var Q30;
            Q30=makeQuery(id+"F4.imprint","IMPRINT",FACE,{"disambiguationData":[TD([[makeQuery(id+"F4.imprint","IMPRINT",EDGE,{"derivedFrom":sQuery(id+"F4.wireOp",EDGE,"E9.7.3.0")}),1.0]])]});
            var Q31;
            Q31=makeQuery(id+"F4.imprint","IMPRINT",FACE,{"disambiguationData":[TD([[makeQuery(id+"F4.imprint","IMPRINT",EDGE,{"derivedFrom":sQuery(id+"F4.wireOp",EDGE,"E9.6.3.0")}),1.0]])]});
            var Q32;
            Q32=makeQuery(id+"F4.imprint","IMPRINT",FACE,{"disambiguationData":[TD([[makeQuery(id+"F4.imprint","IMPRINT",EDGE,{"derivedFrom":sQuery(id+"F4.wireOp",EDGE,"E10.0.8.2")}),1.0]])]});
            var Q33;
            Q33=makeQuery(id+"F4.imprint","IMPRINT",FACE,{"disambiguationData":[TD([[makeQuery(id+"F4.imprint","IMPRINT",EDGE,{"derivedFrom":sQuery(id+"F4.wireOp",EDGE,"E10.0.8.1")}),1.0]])]});
            var Q34;
            Q34=makeQuery(id+"F4.imprint","IMPRINT",FACE,{"disambiguationData":[TD([[makeQuery(id+"F4.imprint","IMPRINT",EDGE,{"derivedFrom":sQuery(id+"F4.wireOp",EDGE,"E10.0.8.0")}),1.0]])]});
            var Q35;
            Q35=makeQuery(id+"F4.imprint","IMPRINT",FACE,{"disambiguationData":[TD([[makeQuery(id+"F4.imprint","IMPRINT",EDGE,{"derivedFrom":sQuery(id+"F4.wireOp",EDGE,"E10.0.9.0")}),1.0]])]});
            var Q36;
            Q36=makeQuery(id+"F4.imprint","IMPRINT",FACE,{"disambiguationData":[TD([[makeQuery(id+"F4.imprint","IMPRINT",EDGE,{"derivedFrom":sQuery(id+"F4.wireOp",EDGE,"E10.0.9.1")}),1.0]])]});
            var Q37;
            Q37=makeQuery(id+"F4.imprint","IMPRINT",FACE,{"disambiguationData":[TD([[makeQuery(id+"F4.imprint","IMPRINT",EDGE,{"derivedFrom":sQuery(id+"F4.wireOp",EDGE,"E10.0.9.2")}),1.0]])]});
            var Q38;
            Q38=makeQuery(id+"F4.imprint","IMPRINT",FACE,{"disambiguationData":[TD([[makeQuery(id+"F4.imprint","IMPRINT",EDGE,{"derivedFrom":sQuery(id+"F4.wireOp",EDGE,"E10.0.9.3")}),1.0]])]});
            var Q39;
            Q39=makeQuery(id+"F4.imprint","IMPRINT",FACE,{"disambiguationData":[TD([[makeQuery(id+"F4.imprint","IMPRINT",EDGE,{"derivedFrom":sQuery(id+"F4.wireOp",EDGE,"c1004ee7-efcd-4f6c-9745-420da8152294.0.9.4")}),1.0]])]});
            var Q40;
            Q40=makeQuery(id+"F4.imprint","IMPRINT",FACE,{"disambiguationData":[TD([[makeQuery(id+"F4.imprint","IMPRINT",EDGE,{"derivedFrom":sQuery(id+"F4.wireOp",EDGE,"E10.0.8.3")}),1.0]])]});
            var Q41;
            Q41=makeQuery(id+"F4.imprint","IMPRINT",FACE,{"disambiguationData":[TD([[makeQuery(id+"F4.imprint","IMPRINT",EDGE,{"derivedFrom":sQuery(id+"F4.wireOp",EDGE,"c1004ee7-efcd-4f6c-9745-420da8152294.0.8.4")}),1.0]])]});
            var Q42;
            Q42=makeQuery(id+"F4.imprint","IMPRINT",FACE,{"disambiguationData":[TD([[makeQuery(id+"F4.imprint","IMPRINT",EDGE,{"derivedFrom":sQuery(id+"F4.wireOp",EDGE,"c1004ee7-efcd-4f6c-9745-420da8152294.0.7.4")}),1.0]])]});
            var Q43;
            Q43=makeQuery(id+"F4.imprint","IMPRINT",FACE,{"disambiguationData":[TD([[makeQuery(id+"F4.imprint","IMPRINT",EDGE,{"derivedFrom":sQuery(id+"F4.wireOp",EDGE,"c1004ee7-efcd-4f6c-9745-420da8152294.0.6.4")}),1.0]])]});
            var Q44;
            Q44=makeQuery(id+"F4.imprint","IMPRINT",FACE,{"disambiguationData":[TD([[makeQuery(id+"F4.imprint","IMPRINT",EDGE,{"derivedFrom":sQuery(id+"F4.wireOp",EDGE,"c1004ee7-efcd-4f6c-9745-420da8152294.0.5.4")}),1.0]])]});
            var Q45;
            Q45=makeQuery(id+"F4.imprint","IMPRINT",FACE,{"disambiguationData":[TD([[makeQuery(id+"F4.imprint","IMPRINT",EDGE,{"derivedFrom":sQuery(id+"F4.wireOp",EDGE,"c1004ee7-efcd-4f6c-9745-420da8152294.0.4.4")}),1.0]])]});
            var Q46;
            Q46=makeQuery(id+"F4.imprint","IMPRINT",FACE,{"disambiguationData":[TD([[makeQuery(id+"F4.imprint","IMPRINT",EDGE,{"derivedFrom":sQuery(id+"F4.wireOp",EDGE,"c1004ee7-efcd-4f6c-9745-420da8152294.0.3.4")}),1.0]])]});
            var Q47;
            Q47=makeQuery(id+"F4.imprint","IMPRINT",FACE,{"disambiguationData":[TD([[makeQuery(id+"F4.imprint","IMPRINT",EDGE,{"derivedFrom":sQuery(id+"F4.wireOp",EDGE,"c1004ee7-efcd-4f6c-9745-420da8152294.0.2.4")}),1.0]])]});
            var Q48;
            Q48=makeQuery(id+"F4.imprint","IMPRINT",FACE,{"disambiguationData":[TD([[makeQuery(id+"F4.imprint","IMPRINT",EDGE,{"derivedFrom":sQuery(id+"F4.wireOp",EDGE,"c1004ee7-efcd-4f6c-9745-420da8152294.0.1.4")}),1.0]])]});
            var Q49;
            Q49=makeQuery(id+"F4.imprint","IMPRINT",FACE,{"disambiguationData":[TD([[makeQuery(id+"F4.imprint","IMPRINT",EDGE,{"derivedFrom":sQuery(id+"F4.wireOp",EDGE,"c1004ee7-efcd-4f6c-9745-420da8152294.0.0.4")}),1.0]])]});
            extrude(context, id + "F5", {"entities" : qUnion([Q0, Q1, Q2, Q3, Q4, Q5, Q6, Q7, Q8, Q9, Q10, Q11, Q12, Q13, Q14, Q15, Q16, Q17, Q18, Q19, Q20, Q21, Q22, Q23, Q24, Q25, Q26, Q27, Q28, Q29, Q30, Q31, Q32, Q33, Q34, Q35, Q36, Q37, Q38, Q39, Q40, Q41, Q42, Q43, Q44, Q45, Q46, Q47, Q48, Q49]), "operationType" : NewBodyOperationType.ADD, "depth" : 1 * mm, "offsetDistance" : 25 * mm});
        }
        {
            var Q0;
            Q0=makeQuery(id+"F5.opExtrude","CAP_FACE",FACE,{"disambiguationData":[OSD([sQuery(id+"F4.wireOp",EDGE,"E7"),sQuery(id+"F4.wireOp",EDGE,"E8")])],"isStart":false});
            var Q1;
            Q1=makeQuery(id+"F5.opExtrude","CAP_FACE",FACE,{"disambiguationData":[OSD([sQuery(id+"F4.wireOp",EDGE,"E9.1.0.0"),sQuery(id+"F4.wireOp",EDGE,"E9.1.0.1")])],"isStart":false});
            var Q2;
            Q2=makeQuery(id+"F5.opExtrude","CAP_FACE",FACE,{"disambiguationData":[OSD([sQuery(id+"F4.wireOp",EDGE,"E9.1.1.0"),sQuery(id+"F4.wireOp",EDGE,"E9.1.1.1")])],"isStart":false});
            var Q3;
            Q3=makeQuery(id+"F5.opExtrude","CAP_FACE",FACE,{"disambiguationData":[OSD([sQuery(id+"F4.wireOp",EDGE,"E9.0.1.0"),sQuery(id+"F4.wireOp",EDGE,"E9.0.1.1")])],"isStart":false});
            var Q4;
            Q4=makeQuery(id+"F5.opExtrude","CAP_FACE",FACE,{"disambiguationData":[OSD([sQuery(id+"F4.wireOp",EDGE,"E9.0.2.0"),sQuery(id+"F4.wireOp",EDGE,"E9.0.2.1")])],"isStart":false});
            var Q5;
            Q5=makeQuery(id+"F5.opExtrude","CAP_FACE",FACE,{"disambiguationData":[OSD([sQuery(id+"F4.wireOp",EDGE,"E9.1.2.0"),sQuery(id+"F4.wireOp",EDGE,"E9.1.2.1")])],"isStart":false});
            var Q6;
            Q6=makeQuery(id+"F5.opExtrude","CAP_FACE",FACE,{"disambiguationData":[OSD([sQuery(id+"F4.wireOp",EDGE,"E9.0.3.0"),sQuery(id+"F4.wireOp",EDGE,"E9.0.3.1")])],"isStart":false});
            var Q7;
            Q7=makeQuery(id+"F5.opExtrude","CAP_FACE",FACE,{"disambiguationData":[OSD([sQuery(id+"F4.wireOp",EDGE,"E9.1.3.0"),sQuery(id+"F4.wireOp",EDGE,"E9.1.3.1")])],"isStart":false});
            var Q8;
            Q8=makeQuery(id+"F5.opExtrude","CAP_FACE",FACE,{"disambiguationData":[OSD([sQuery(id+"F4.wireOp",EDGE,"E9.2.3.0"),sQuery(id+"F4.wireOp",EDGE,"E9.2.3.1")])],"isStart":false});
            var Q9;
            Q9=makeQuery(id+"F5.opExtrude","CAP_FACE",FACE,{"disambiguationData":[OSD([sQuery(id+"F4.wireOp",EDGE,"E9.2.2.0"),sQuery(id+"F4.wireOp",EDGE,"E9.2.2.1")])],"isStart":false});
            var Q10;
            Q10=makeQuery(id+"F5.opExtrude","CAP_FACE",FACE,{"disambiguationData":[OSD([sQuery(id+"F4.wireOp",EDGE,"E9.2.1.0"),sQuery(id+"F4.wireOp",EDGE,"E9.2.1.1")])],"isStart":false});
            var Q11;
            Q11=makeQuery(id+"F5.opExtrude","CAP_FACE",FACE,{"disambiguationData":[OSD([sQuery(id+"F4.wireOp",EDGE,"E9.2.0.0"),sQuery(id+"F4.wireOp",EDGE,"E9.2.0.1")])],"isStart":false});
            var Q12;
            Q12=makeQuery(id+"F5.opExtrude","CAP_FACE",FACE,{"disambiguationData":[OSD([sQuery(id+"F4.wireOp",EDGE,"E9.4.0.0"),sQuery(id+"F4.wireOp",EDGE,"E9.4.0.1")])],"isStart":false});
            var Q13;
            Q13=makeQuery(id+"F5.opExtrude","CAP_FACE",FACE,{"disambiguationData":[OSD([sQuery(id+"F4.wireOp",EDGE,"E9.5.1.0"),sQuery(id+"F4.wireOp",EDGE,"E9.5.1.1")])],"isStart":false});
            var Q14;
            Q14=makeQuery(id+"F5.opExtrude","CAP_FACE",FACE,{"disambiguationData":[OSD([sQuery(id+"F4.wireOp",EDGE,"E9.4.1.0"),sQuery(id+"F4.wireOp",EDGE,"E9.4.1.1")])],"isStart":false});
            var Q15;
            Q15=makeQuery(id+"F5.opExtrude","CAP_FACE",FACE,{"disambiguationData":[OSD([sQuery(id+"F4.wireOp",EDGE,"E9.5.2.0"),sQuery(id+"F4.wireOp",EDGE,"E9.5.2.1")])],"isStart":false});
            var Q16;
            Q16=makeQuery(id+"F5.opExtrude","CAP_FACE",FACE,{"disambiguationData":[OSD([sQuery(id+"F4.wireOp",EDGE,"E9.4.2.0"),sQuery(id+"F4.wireOp",EDGE,"E9.4.2.1")])],"isStart":false});
            var Q17;
            Q17=makeQuery(id+"F5.opExtrude","CAP_FACE",FACE,{"disambiguationData":[OSD([sQuery(id+"F4.wireOp",EDGE,"E9.5.3.0"),sQuery(id+"F4.wireOp",EDGE,"E9.5.3.1")])],"isStart":false});
            var Q18;
            Q18=makeQuery(id+"F5.opExtrude","CAP_FACE",FACE,{"disambiguationData":[OSD([sQuery(id+"F4.wireOp",EDGE,"E9.4.3.0"),sQuery(id+"F4.wireOp",EDGE,"E9.4.3.1")])],"isStart":false});
            var Q19;
            Q19=makeQuery(id+"F5.opExtrude","CAP_FACE",FACE,{"disambiguationData":[OSD([sQuery(id+"F4.wireOp",EDGE,"E9.6.3.0"),sQuery(id+"F4.wireOp",EDGE,"E9.6.3.1")])],"isStart":false});
            var Q20;
            Q20=makeQuery(id+"F5.opExtrude","CAP_FACE",FACE,{"disambiguationData":[OSD([sQuery(id+"F4.wireOp",EDGE,"E9.6.2.0"),sQuery(id+"F4.wireOp",EDGE,"E9.6.2.1")])],"isStart":false});
            var Q21;
            Q21=makeQuery(id+"F5.opExtrude","CAP_FACE",FACE,{"disambiguationData":[OSD([sQuery(id+"F4.wireOp",EDGE,"E9.6.1.0"),sQuery(id+"F4.wireOp",EDGE,"E9.6.1.1")])],"isStart":false});
            var Q22;
            Q22=makeQuery(id+"F5.opExtrude","CAP_FACE",FACE,{"disambiguationData":[OSD([sQuery(id+"F4.wireOp",EDGE,"E9.6.0.0"),sQuery(id+"F4.wireOp",EDGE,"E9.6.0.1")])],"isStart":false});
            var Q23;
            Q23=makeQuery(id+"F5.opExtrude","CAP_FACE",FACE,{"disambiguationData":[OSD([sQuery(id+"F4.wireOp",EDGE,"E9.7.0.0"),sQuery(id+"F4.wireOp",EDGE,"E9.7.0.1")])],"isStart":false});
            var Q24;
            Q24=makeQuery(id+"F5.opExtrude","CAP_FACE",FACE,{"disambiguationData":[OSD([sQuery(id+"F4.wireOp",EDGE,"E9.7.1.0"),sQuery(id+"F4.wireOp",EDGE,"E9.7.1.1")])],"isStart":false});
            var Q25;
            Q25=makeQuery(id+"F5.opExtrude","CAP_FACE",FACE,{"disambiguationData":[OSD([sQuery(id+"F4.wireOp",EDGE,"E9.7.2.0"),sQuery(id+"F4.wireOp",EDGE,"E9.7.2.1")])],"isStart":false});
            var Q26;
            Q26=makeQuery(id+"F5.opExtrude","CAP_FACE",FACE,{"disambiguationData":[OSD([sQuery(id+"F4.wireOp",EDGE,"E9.7.3.0"),sQuery(id+"F4.wireOp",EDGE,"E9.7.3.1")])],"isStart":false});
            var Q27;
            Q27=makeQuery(id+"F5.opExtrude","CAP_EDGE",EDGE,{"disambiguationData":[OSD([sQuery(id+"F4.wireOp",EDGE,"E9.3.0.0")])],"isStart":false});
            var Q28;
            Q28=makeQuery(id+"F5.opExtrude","CAP_EDGE",EDGE,{"disambiguationData":[OSD([sQuery(id+"F4.wireOp",EDGE,"E9.3.0.1")])],"isStart":false});
            var Q29;
            Q29=makeQuery(id+"F5.opExtrude","CAP_FACE",FACE,{"disambiguationData":[OSD([sQuery(id+"F4.wireOp",EDGE,"E9.3.1.0"),sQuery(id+"F4.wireOp",EDGE,"E9.3.1.1")])],"isStart":false});
            var Q30;
            Q30=makeQuery(id+"F5.opExtrude","CAP_FACE",FACE,{"disambiguationData":[OSD([sQuery(id+"F4.wireOp",EDGE,"E9.3.2.0"),sQuery(id+"F4.wireOp",EDGE,"E9.3.2.1")])],"isStart":false});
            var Q31;
            Q31=makeQuery(id+"F5.opExtrude","CAP_FACE",FACE,{"disambiguationData":[OSD([sQuery(id+"F4.wireOp",EDGE,"E9.3.3.0"),sQuery(id+"F4.wireOp",EDGE,"E9.3.3.1")])],"isStart":false});
            var Q32;
            Q32=makeQuery(id+"F5.opExtrude","CAP_FACE",FACE,{"disambiguationData":[OSD([sQuery(id+"F4.wireOp",EDGE,"E9.5.0.0"),sQuery(id+"F4.wireOp",EDGE,"E9.5.0.1")])],"isStart":false});
            fillet(context, id + "F6", {"entities" : qUnion([Q0, Q1, Q2, Q3, Q4, Q5, Q6, Q7, Q8, Q9, Q10, Q11, Q12, Q13, Q14, Q15, Q16, Q17, Q18, Q19, Q20, Q21, Q22, Q23, Q24, Q25, Q26, Q27, Q28, Q29, Q30, Q31, Q32]), "radius" : 0.5 * mm, "tangentPropagation" : true, "allowEdgeOverflow" : false});
        }
    });
